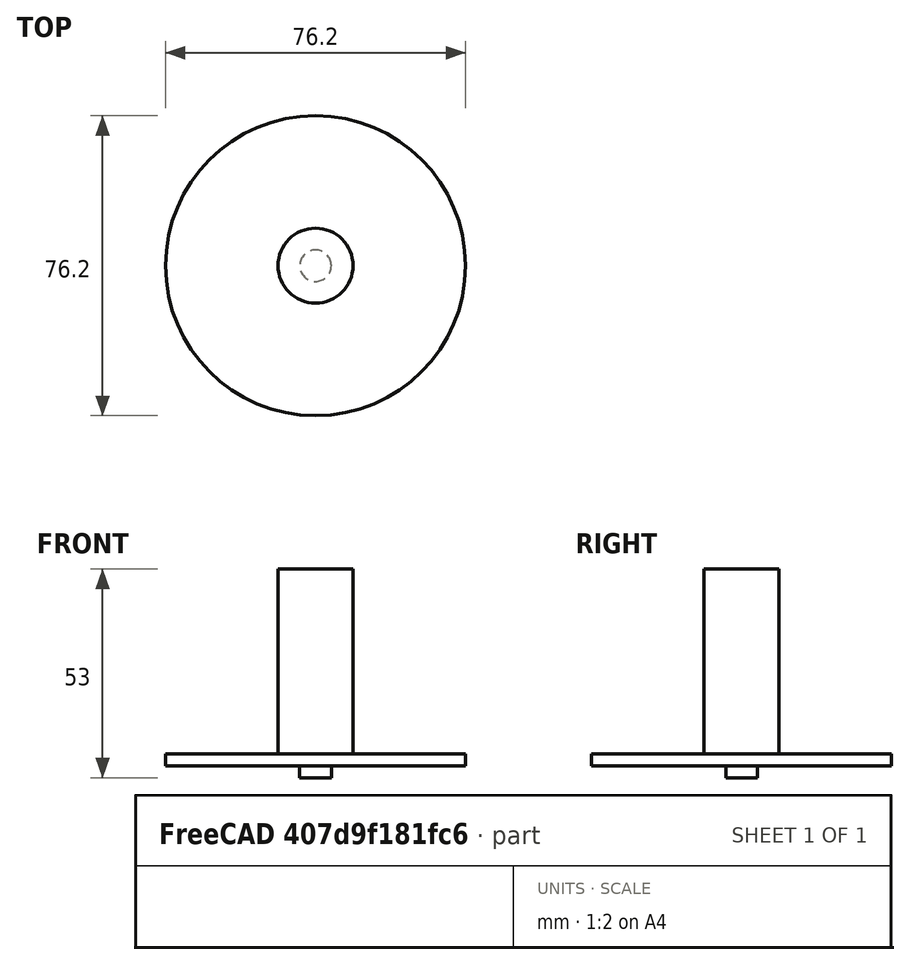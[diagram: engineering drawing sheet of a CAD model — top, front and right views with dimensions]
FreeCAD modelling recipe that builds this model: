
FCSTD DOCUMENT  (FreeCAD 1.0R39109 (Git))
Label: slittingsaw
License: All rights reserved
LicenseURL: http://en.wikipedia.org/wiki/All_rights_reserved
objects: Sketcher::SketchObject×1, PartDesign::Revolution×1, App::FeaturePython×1, PartDesign::Body×1
note: 6 computed .brp shape members not serialized (recipe doc carries the construction recipe); baked Part::Feature solids carry a one-line shape summary decoded from their .brp

FEATURE [Sketcher::SketchObject] Sketch
  ArcFitTolerance = 0
  AttachmentSupport = -> [XZ_Plane]
  FullyConstrained = true
  MakeInternals = false
  MapMode = 5
  Placement = pos=(0,0,0) rot=(1,0,0;1.5708rad)
  expr: Constraints[18] = <<Attributes>>.CapDiameter
  expr: Constraints[20] = <<Attributes>>.CapHeight
  expr: Constraints[21] = <<Attributes>>.BladeThickness
  expr: Constraints[22] = <<Attributes>>.Diameter
  expr: Constraints[2] = <<Attributes>>.Length
  expr: Constraints[8] = <<Attributes>>.ShankDiameter
  sketch-geometry (11):
    g0: LineSegment StartX=0 StartY=50 StartZ=0 EndX=0 EndY=-3 EndZ=0
    g1: LineSegment StartX=9.525 StartY=50 StartZ=0 EndX=0 EndY=50 EndZ=0
    g2: LineSegment [constr] StartX=38.1 StartY=0 StartZ=0 EndX=-38.1 EndY=0 EndZ=0
    g3: LineSegment StartX=9.525 StartY=3 StartZ=0 EndX=38.1 EndY=3 EndZ=0
    g4: LineSegment StartX=9.525 StartY=50 StartZ=0 EndX=9.525 EndY=3 EndZ=0
    g5: LineSegment [constr] StartX=-9.525 StartY=50 StartZ=0 EndX=9.525 EndY=50 EndZ=0
    g6: LineSegment StartX=38.1 StartY=3 StartZ=0 EndX=38.1 EndY=0 EndZ=0
    g7: LineSegment StartX=38.1 StartY=0 StartZ=0 EndX=4 EndY=0 EndZ=0
    g8: LineSegment StartX=4 StartY=0 StartZ=0 EndX=4 EndY=-3 EndZ=0
    g9: LineSegment StartX=4 StartY=-3 StartZ=0 EndX=0 EndY=-3 EndZ=0
    g10: LineSegment [constr] StartX=-4 StartY=-3 StartZ=0 EndX=4 EndY=-3 EndZ=0
  constraints (30):
    c: Vertical(g0)
    c: Symmetric(g6,g2,g0)
    c: DistanceY(g6,g1) = 50
    c: Horizontal(g3)
    c: Vertical(g4)
    c: Coincident(g1,g4)
    c: Symmetric(g5,g5,g0)
    c: Coincident(g5,g1)
    c: DistanceX(g5,g5) = 19.05
    c: Coincident(g3,g4)
    c: Coincident(g3,g6)
    c: Vertical(g6)
    c: Coincident(g6,g7)
    c: Horizontal(g7)
    c: Coincident(g8,g9)
    c: Horizontal(g9)
    c: Vertical(g8)
    c: Coincident(g10,g8)
    c: DistanceX(g10,g10) = 8
    c: Symmetric(g10,g8,g-2)
    c: DistanceY(g8,g8) = 3
    c: DistanceY(g6,g6) = 3
    c: DistanceX(g2,g2) = 76.2
    c: Coincident(g7,g8)
    c: Coincident(g2,g6)
    c: Coincident(g0,g9)
    c: Coincident(g0,g1)
    c: Horizontal(g1)
    c: PointOnObject(g0,g-2)
    c: PointOnObject(g7,g-1)
FEATURE [PartDesign::Revolution] Revolution
  AllowMultiFace = false
  Angle = 360
  Angle2 = 60
  Axis = (0,2e-16,1)
  Base = (0,0,0)
  Placement = pos=(0,0,0) rot=(1,0,0;1.5708rad)
  Profile = -> Sketch
  ReferenceAxis = -> Sketch [V_Axis]
  Reversed = true
  Suppressed = false
  Type = 0
FEATURE [App::FeaturePython] PropertyBag  label="Attributes"  # WARN: FeaturePython — macro-defined, semantics opaque (R4)
  BladeThickness = 3
  CapDiameter = 8
  CapHeight = 3
  CustomPropertyGroups = 0
  Diameter = 100
  Flutes = 20
  Length = 50
  ShankDiameter = 15
FEATURE [PartDesign::Body] Body  label="SlittingSaw"
  AllowCompound = false
  Group = -> [Sketch,Revolution,PropertyBag]
  Origin = -> Origin
  Tip = -> Revolution
